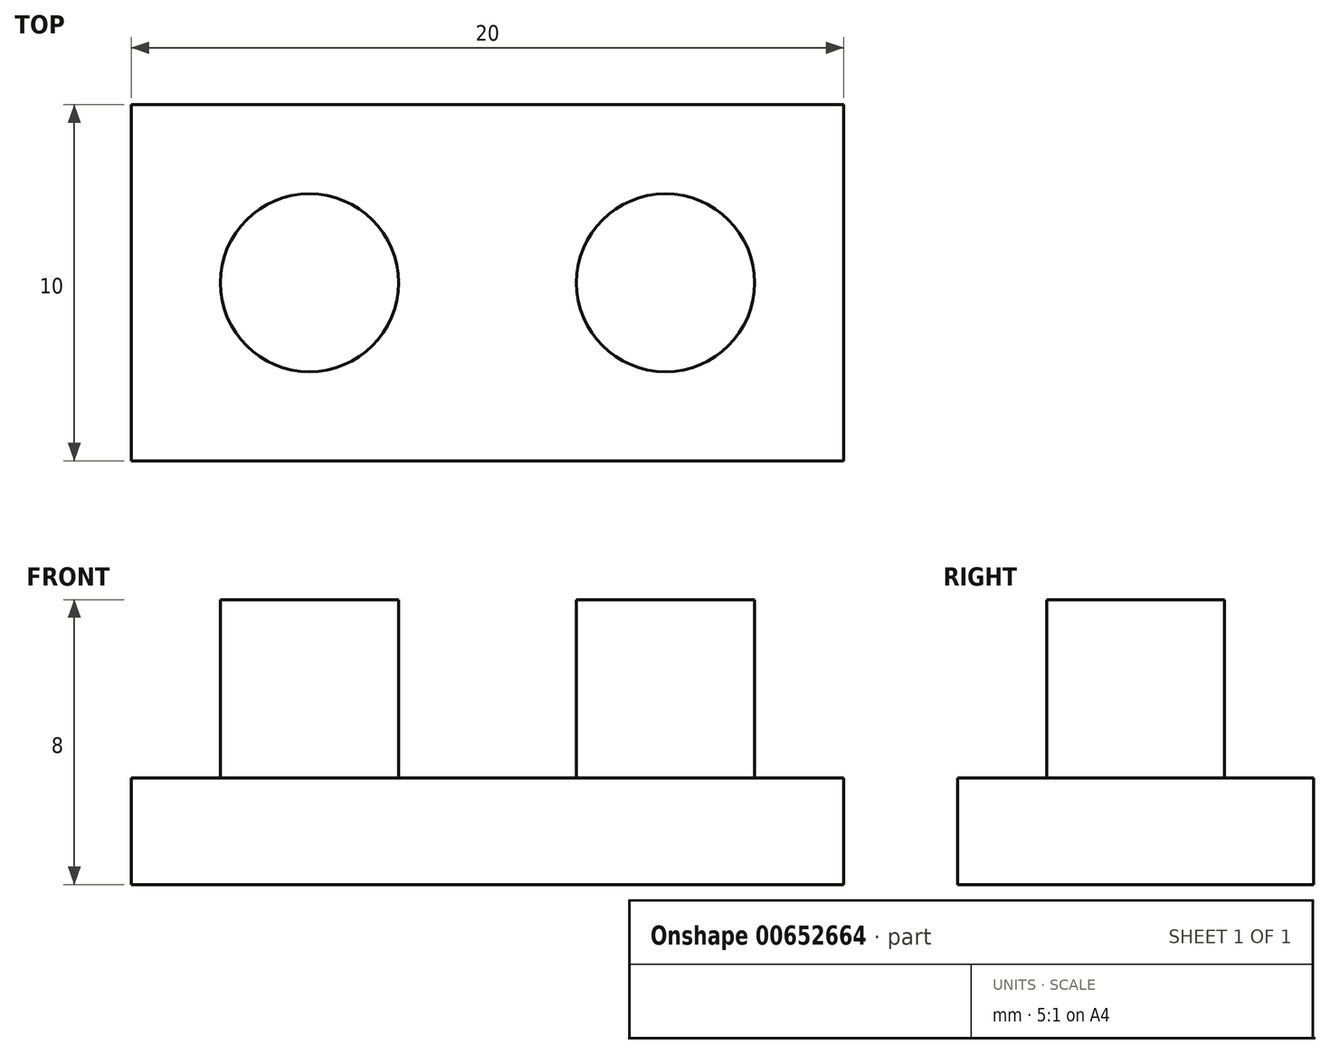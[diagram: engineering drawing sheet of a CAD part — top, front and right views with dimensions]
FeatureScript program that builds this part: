
annotation { "Feature Type Name" : "Feature", "Feature Type Description" : "" }
export const myFeature = defineFeature(function(context is Context, id is Id, definition is map)
    precondition{}
    {
        {
            var Q0;
            Q0=qCreatedBy(makeId("Top.planeOp"),FACE);
            var sketch = newSketch(context, id + "F0", { "sketchPlane" : qUnion([Q0])});
            skLineSegment(sketch, "E0.bottom", {"start": v(10, -5) * mm, "end": v(-10, -5) * mm});
            skLineSegment(sketch, "E0.top", {"start": v(10, 5) * mm, "end": v(-10, 5) * mm});
            skLineSegment(sketch, "E0.left", {"start": v(10, -5) * mm, "end": v(10, 5) * mm});
            skLineSegment(sketch, "E0.right", {"start": v(-10, -5) * mm, "end": v(-10, 5) * mm});
            skPoint(sketch, "E0.middle", {"position": v(0, 0) * mm});
            skLineSegment(sketch, "E1", {"start": v(-5, 5) * mm, "end": v(-5, 0) * mm, "construction": true});
            skLineSegment(sketch, "E2", {"start": v(-5, 0) * mm, "end": v(-10, 0) * mm, "construction": true});
            skLineSegment(sketch, "E3", {"start": v(10, 0) * mm, "end": v(5, 0) * mm, "construction": true});
            skLineSegment(sketch, "E4", {"start": v(5, 0) * mm, "end": v(5, 5) * mm, "construction": true});
            skSolve(sketch);
        }
        {
            var Q0;
            Q0=makeQuery(id+"F0.imprint","IMPRINT",FACE,{"disambiguationData":[TD([[makeQuery(id+"F0.imprint","IMPRINT",EDGE,{"derivedFrom":sQuery(id+"F0.wireOp",EDGE,"E0.bottom")}),-1.0]])]});
            extrude(context, id + "F1", {"entities" : qUnion([Q0]), "depth" : 3 * mm, "offsetDistance" : 25 * mm});
        }
        {
            var Q0;
            Q0=makeQuery(id+"F1.opExtrude","CAP_FACE",FACE,{"disambiguationData":[OSD([sQuery(id+"F0.wireOp",EDGE,"E0.bottom"),sQuery(id+"F0.wireOp",EDGE,"E0.top"),sQuery(id+"F0.wireOp",EDGE,"E0.left"),sQuery(id+"F0.wireOp",EDGE,"E0.right")])],"isStart":false});
            var sketch = newSketch(context, id + "F2", { "sketchPlane" : qUnion([Q0])});
            skLineSegment(sketch, "E5", {"start": v(-10, 0) * mm, "end": v(-5, 0) * mm, "construction": true});
            skLineSegment(sketch, "E6", {"start": v(-5, 0) * mm, "end": v(-5, 5) * mm, "construction": true});
            skLineSegment(sketch, "E7", {"start": v(10, 0) * mm, "end": v(5, 0) * mm, "construction": true});
            skLineSegment(sketch, "E8", {"start": v(5, 0) * mm, "end": v(5, 5) * mm, "construction": true});
            skCircle(sketch, "E9", {"center": v(-5, 0) * mm, "radius": 2.5 * mm});
            skCircle(sketch, "E10", {"center": v(5, 0) * mm, "radius": 2.5 * mm});
            skSolve(sketch);
        }
        {
            var Q0;
            Q0=makeQuery(id+"F2.imprint","IMPRINT",FACE,{"disambiguationData":[TD([[makeQuery(id+"F2.imprint","IMPRINT",EDGE,{"derivedFrom":sQuery(id+"F2.wireOp",EDGE,"E10")}),1.0]])]});
            var Q1;
            Q1=makeQuery(id+"F2.imprint","IMPRINT",FACE,{"disambiguationData":[TD([[makeQuery(id+"F2.imprint","IMPRINT",EDGE,{"derivedFrom":sQuery(id+"F2.wireOp",EDGE,"E9")}),1.0]])]});
            extrude(context, id + "F3", {"entities" : qUnion([Q0, Q1]), "operationType" : NewBodyOperationType.ADD, "depth" : 5 * mm, "offsetDistance" : 25 * mm});
        }
    });
